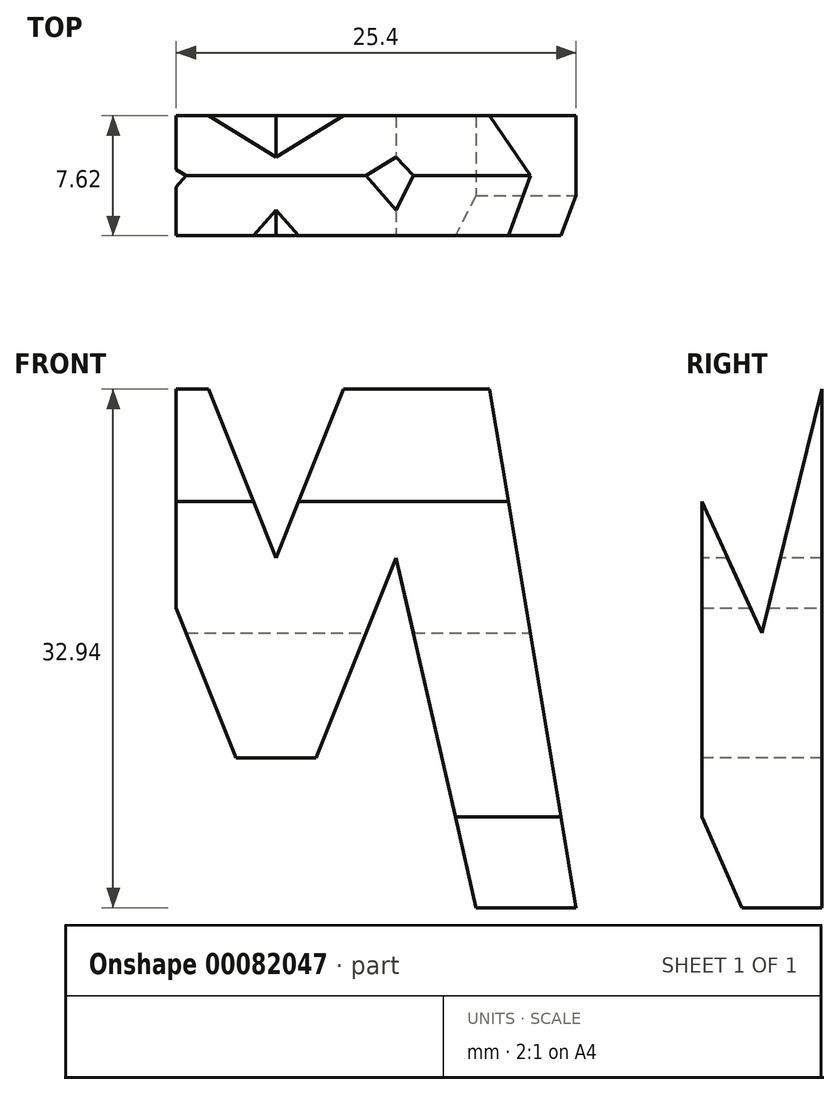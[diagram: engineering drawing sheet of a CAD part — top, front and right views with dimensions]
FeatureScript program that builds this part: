
annotation { "Feature Type Name" : "Feature", "Feature Type Description" : "" }
export const myFeature = defineFeature(function(context is Context, id is Id, definition is map)
    precondition{}
    {
        {
            var Q0;
            Q0=qCreatedBy(makeId("Front.planeOp"),FACE);
            var sketch = newSketch(context, id + "F0", { "sketchPlane" : qUnion([Q0])});
            skLineSegment(sketch, "E0", {"start": v(0, 0) * mm, "end": v(38.1, 0) * mm});
            skLineSegment(sketch, "E1", {"start": v(38.1, 0) * mm, "end": v(38.1, 38.1) * mm});
            skLineSegment(sketch, "E2", {"start": v(38.1, 38.1) * mm, "end": v(0, 38.1) * mm});
            skLineSegment(sketch, "E3", {"start": v(0, 38.1) * mm, "end": v(0, 0) * mm});
            skSolve(sketch);
        }
        {
            var Q0;
            Q0=makeQuery(id+"F0.imprint","IMPRINT",FACE,{"disambiguationData":[TD([[makeQuery(id+"F0.imprint","IMPRINT",EDGE,{"derivedFrom":sQuery(id+"F0.wireOp",EDGE,"E0")}),1.0]])]});
            extrude(context, id + "F1", {"entities" : qUnion([Q0]), "depth" : 38.1 * mm});
        }
        {
            var Q0;
            Q0=qCreatedBy(makeId("Front.planeOp"),FACE);
            cPlane(context, id + "F2", {"entities" : qUnion([Q0]), "cplaneType" : CPlaneType.OFFSET, "offset" : 38.1 * mm, "width" : 152.4 * mm, "height" : 152.4 * mm});
        }
        {
            var Q0;
            Q0=qCreatedBy(makeId("Right.planeOp"),FACE);
            cPlane(context, id + "F3", {"entities" : qUnion([Q0]), "cplaneType" : CPlaneType.OFFSET, "offset" : 38.1 * mm, "width" : 152.4 * mm, "height" : 152.4 * mm});
        }
        {
            var Q0;
            Q0=qCreatedBy(makeId("Top.planeOp"),FACE);
            cPlane(context, id + "F4", {"entities" : qUnion([Q0]), "cplaneType" : CPlaneType.OFFSET, "offset" : 38.1 * mm, "width" : 152.4 * mm, "height" : 152.4 * mm});
        }
        {
            var Q0;
            Q0=qCreatedBy(id+"F3.planeOp",FACE);
            var sketch = newSketch(context, id + "F5", { "sketchPlane" : qUnion([Q0])});
            skLineSegment(sketch, "E4", {"start": v(-38.1, 38.1) * mm, "end": v(-31.75, 0) * mm});
            skLineSegment(sketch, "E5", {"start": v(-31.75, 0) * mm, "end": v(-25.4, 0) * mm});
            skLineSegment(sketch, "E6", {"start": v(-25.4, 0) * mm, "end": v(-19.67, 15.88) * mm});
            skLineSegment(sketch, "E7", {"start": v(-19.67, 15.88) * mm, "end": v(-12.7, 0) * mm});
            skLineSegment(sketch, "E8", {"start": v(-12.7, 0) * mm, "end": v(-6.35, 0) * mm});
            skLineSegment(sketch, "E9", {"start": v(-6.35, 0) * mm, "end": v(0, 38.1) * mm});
            skLineSegment(sketch, "E10", {"start": v(0, 38.1) * mm, "end": v(-6.35, 38.1) * mm});
            skLineSegment(sketch, "E11", {"start": v(-6.35, 38.1) * mm, "end": v(-11.43, 17.45) * mm});
            skLineSegment(sketch, "E12", {"start": v(-11.43, 17.45) * mm, "end": v(-16.5, 28.58) * mm});
            skLineSegment(sketch, "E13", {"start": v(-16.5, 28.58) * mm, "end": v(-21.59, 28.58) * mm});
            skLineSegment(sketch, "E14", {"start": v(-21.59, 28.58) * mm, "end": v(-26.67, 16.45) * mm});
            skLineSegment(sketch, "E15", {"start": v(-26.67, 16.45) * mm, "end": v(-31.75, 38.1) * mm});
            skLineSegment(sketch, "E16", {"start": v(-31.75, 38.1) * mm, "end": v(-38.1, 38.1) * mm});
            skLineSegment(sketch, "E17.bottom", {"start": v(0, 0) * mm, "end": v(-38.1, 0) * mm});
            skLineSegment(sketch, "E17.top", {"start": v(0, 38.1) * mm, "end": v(-38.1, 38.1) * mm});
            skLineSegment(sketch, "E17.left", {"start": v(0, 0) * mm, "end": v(0, 38.1) * mm});
            skLineSegment(sketch, "E17.right", {"start": v(-38.1, 0) * mm, "end": v(-38.1, 38.1) * mm});
            skSolve(sketch);
        }
        {
            var Q0;
            {var subQ0=sQuery(id+"F5.wireOp",EDGE,"E4");Q0=makeQuery(id+"F5.imprint","IMPRINT",FACE,{"disambiguationData":[TD([[makeQuery(id+"F5.imprint","IMPRINT",EDGE,{"derivedFrom":subQ0}),-1.0]])]});}
            var Q1;
            {var subQ0=sQuery(id+"F5.wireOp",EDGE,"E6");Q1=makeQuery(id+"F5.imprint","IMPRINT",FACE,{"disambiguationData":[TD([[makeQuery(id+"F5.imprint","IMPRINT",EDGE,{"derivedFrom":subQ0}),-1.0]])]});}
            var Q2;
            {var subQ1=sQuery(id+"F5.wireOp",EDGE,"E11");Q2=makeQuery(id+"F5.imprint","IMPRINT",FACE,{"disambiguationData":[TD([[makeQuery(id+"F5.imprint","IMPRINT",EDGE,{"derivedFrom":subQ1}),-1.0]])]});}
            var Q3;
            {var subQ0=sQuery(id+"F5.wireOp",EDGE,"E9");Q3=makeQuery(id+"F5.imprint","IMPRINT",FACE,{"disambiguationData":[TD([[makeQuery(id+"F5.imprint","IMPRINT",EDGE,{"derivedFrom":subQ0}),-1.0]])]});}
            extrude(context, id + "F6", {"entities" : qUnion([Q0, Q1, Q2, Q3]), "operationType" : NewBodyOperationType.REMOVE, "oppositeDirection" : true, "depth" : 38.1 * mm});
        }
        {
            var Q0;
            Q0=qCreatedBy(id+"F2.planeOp",FACE);
            var sketch = newSketch(context, id + "F7", { "sketchPlane" : qUnion([Q0])});
            skLineSegment(sketch, "E18", {"start": v(0, 0) * mm, "end": v(38.1, 0) * mm});
            skLineSegment(sketch, "E19", {"start": v(38.1, 0) * mm, "end": v(38.1, 38.1) * mm});
            skLineSegment(sketch, "E20", {"start": v(38.1, 38.1) * mm, "end": v(0, 38.1) * mm});
            skLineSegment(sketch, "E21", {"start": v(0, 38.1) * mm, "end": v(0, 0) * mm});
            skLineSegment(sketch, "E22", {"start": v(0, 0) * mm, "end": v(6.35, 38.1) * mm});
            skLineSegment(sketch, "E23", {"start": v(6.35, 38.1) * mm, "end": v(12.7, 38.1) * mm});
            skLineSegment(sketch, "E24", {"start": v(12.7, 38.1) * mm, "end": v(19.05, 22.23) * mm});
            skLineSegment(sketch, "E25", {"start": v(19.05, 22.23) * mm, "end": v(25.4, 38.1) * mm});
            skLineSegment(sketch, "E26", {"start": v(25.4, 38.1) * mm, "end": v(31.75, 38.1) * mm});
            skLineSegment(sketch, "E27", {"start": v(31.75, 38.1) * mm, "end": v(38.1, 0) * mm});
            skLineSegment(sketch, "E28", {"start": v(31.75, 0) * mm, "end": v(26.67, 22.23) * mm});
            skLineSegment(sketch, "E29", {"start": v(26.67, 22.23) * mm, "end": v(21.59, 9.52) * mm});
            skLineSegment(sketch, "E30", {"start": v(21.59, 9.52) * mm, "end": v(16.51, 9.52) * mm});
            skLineSegment(sketch, "E31", {"start": v(16.5, 9.52) * mm, "end": v(11.43, 22.23) * mm});
            skLineSegment(sketch, "E32", {"start": v(11.43, 22.23) * mm, "end": v(6.35, 0) * mm});
            skLineSegment(sketch, "E33", {"start": v(6.35, 0) * mm, "end": v(0, 0) * mm});
            skSolve(sketch);
        }
        {
            var Q0;
            {var subQ0=sQuery(id+"F7.wireOp",EDGE,"E21");Q0=makeQuery(id+"F7.imprint","IMPRINT",FACE,{"disambiguationData":[TD([[makeQuery(id+"F7.imprint","IMPRINT",EDGE,{"derivedFrom":subQ0}),1.0]])]});}
            var Q1;
            {var subQ0=sQuery(id+"F7.wireOp",EDGE,"E24");Q1=makeQuery(id+"F7.imprint","IMPRINT",FACE,{"disambiguationData":[TD([[makeQuery(id+"F7.imprint","IMPRINT",EDGE,{"derivedFrom":subQ0}),1.0]])]});}
            var Q2;
            {var subQ2=sQuery(id+"F7.wireOp",EDGE,"E28");Q2=makeQuery(id+"F7.imprint","IMPRINT",FACE,{"disambiguationData":[TD([[makeQuery(id+"F7.imprint","IMPRINT",EDGE,{"derivedFrom":subQ2}),1.0]])]});}
            var Q3;
            {var subQ0=sQuery(id+"F7.wireOp",EDGE,"E19");Q3=makeQuery(id+"F7.imprint","IMPRINT",FACE,{"disambiguationData":[TD([[makeQuery(id+"F7.imprint","IMPRINT",EDGE,{"derivedFrom":subQ0}),1.0]])]});}
            extrude(context, id + "F8", {"entities" : qUnion([Q0, Q1, Q2, Q3]), "operationType" : NewBodyOperationType.REMOVE, "oppositeDirection" : true, "depth" : 38.1 * mm});
        }
        {
            var Q0;
            Q0=qCreatedBy(id+"F4.planeOp",FACE);
            var sketch = newSketch(context, id + "F9", { "sketchPlane" : qUnion([Q0])});
            skLineSegment(sketch, "E34", {"start": v(0, 0) * mm, "end": v(38.1, 0) * mm});
            skLineSegment(sketch, "E35", {"start": v(38.1, 0) * mm, "end": v(38.1, -38.1) * mm});
            skLineSegment(sketch, "E36", {"start": v(38.1, -38.1) * mm, "end": v(0, -38.1) * mm});
            skLineSegment(sketch, "E37", {"start": v(0, -38.1) * mm, "end": v(0, 0) * mm});
            skLineSegment(sketch, "E38", {"start": v(38.1, 0) * mm, "end": v(0, 0) * mm});
            skLineSegment(sketch, "E39", {"start": v(0, -22.86) * mm, "end": v(25.4, -22.86) * mm});
            skLineSegment(sketch, "E40", {"start": v(25.4, -22.86) * mm, "end": v(25.4, -30.48) * mm});
            skLineSegment(sketch, "E41", {"start": v(25.4, -30.48) * mm, "end": v(0, -30.48) * mm});
            skLineSegment(sketch, "E42", {"start": v(0, -30.48) * mm, "end": v(0, -38.1) * mm});
            skLineSegment(sketch, "E43", {"start": v(38.1, -38.1) * mm, "end": v(38.1, -15.24) * mm});
            skLineSegment(sketch, "E44", {"start": v(38.1, -15.24) * mm, "end": v(12.7, -15.24) * mm});
            skLineSegment(sketch, "E45", {"start": v(12.7, -15.24) * mm, "end": v(12.7, -7.62) * mm});
            skLineSegment(sketch, "E46", {"start": v(12.7, -7.62) * mm, "end": v(38.1, -7.62) * mm});
            skLineSegment(sketch, "E47", {"start": v(38.1, -7.62) * mm, "end": v(38.1, 0) * mm});
            skSolve(sketch);
        }
        {
            var Q0;
            Q0=makeQuery(id+"F9.imprint","IMPRINT",FACE,{"disambiguationData":[TD([[makeQuery(id+"F9.imprint","IMPRINT",EDGE,{"derivedFrom":sQuery(id+"F9.wireOp",EDGE,"E35")}),-1.0]])]});
            var Q1;
            {var subQ2=sQuery(id+"F9.wireOp",EDGE,"E39");Q1=makeQuery(id+"F9.imprint","IMPRINT",FACE,{"disambiguationData":[TD([[makeQuery(id+"F9.imprint","IMPRINT",EDGE,{"derivedFrom":subQ2}),-1.0]])]});}
            extrude(context, id + "F10", {"entities" : qUnion([Q0, Q1]), "operationType" : NewBodyOperationType.REMOVE, "oppositeDirection" : true, "depth" : 38.1 * mm});
        }
    });
